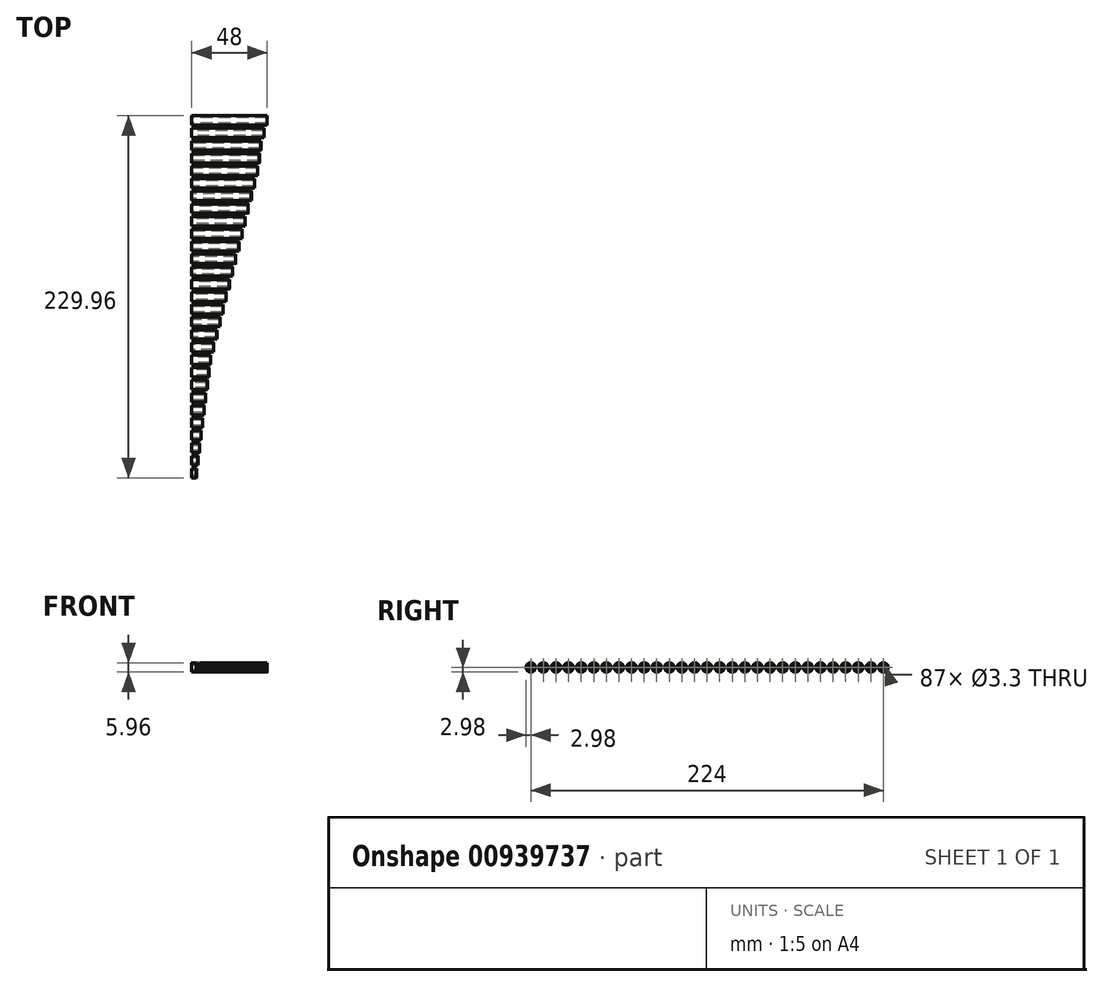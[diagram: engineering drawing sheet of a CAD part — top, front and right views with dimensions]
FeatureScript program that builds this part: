
annotation { "Feature Type Name" : "Feature", "Feature Type Description" : "" }
export const myFeature = defineFeature(function(context is Context, id is Id, definition is map)
    precondition{}
    {
        {
            var Q0;
            Q0=qCreatedBy(makeId("Right.planeOp"),FACE);
            var sketch = newSketch(context, id + "F0", { "sketchPlane" : qUnion([Q0])});
            skCircle(sketch, "E0", {"center": v(0, 0) * mm, "radius": 1.65 * mm});
            skCircle(sketch, "E1", {"center": v(0, 0) * mm, "radius": 2.98 * mm});
            skSolve(sketch);
        }
        {
            var Q0;
            Q0=qSketchRegion(id+"F0",true);
            extrude(context, id + "F1", {"entities" : qUnion([Q0]), "depth" : 3 * mm, "offsetDistance" : 25 * mm});
        }
        {
            var Q0;
            Q0=qSketchRegion(id+"F0",true);
            extrude(context, id + "F2", {"entities" : qUnion([Q0]), "depth" : 4 * mm, "offsetDistance" : 25 * mm});
        }
        {
            var Q0;
            Q0=qSketchRegion(id+"F0",true);
            extrude(context, id + "F3", {"entities" : qUnion([Q0]), "depth" : 5 * mm, "offsetDistance" : 25 * mm});
        }
        {
            var Q0;
            Q0=qSketchRegion(id+"F0",true);
            extrude(context, id + "F4", {"entities" : qUnion([Q0]), "depth" : 6 * mm, "offsetDistance" : 25 * mm});
        }
        {
            var Q0;
            Q0=qSketchRegion(id+"F0",true);
            extrude(context, id + "F5", {"entities" : qUnion([Q0]), "depth" : 7 * mm, "offsetDistance" : 25 * mm});
        }
        {
            var Q0;
            Q0=qSketchRegion(id+"F0",true);
            extrude(context, id + "F6", {"entities" : qUnion([Q0]), "depth" : 8 * mm, "offsetDistance" : 25 * mm});
        }
        {
            var Q0;
            Q0=qSketchRegion(id+"F0",true);
            extrude(context, id + "F7", {"entities" : qUnion([Q0]), "depth" : 9 * mm, "offsetDistance" : 25 * mm});
        }
        {
            var Q0;
            Q0=qSketchRegion(id+"F0",true);
            extrude(context, id + "F8", {"entities" : qUnion([Q0]), "depth" : 10 * mm, "offsetDistance" : 25 * mm});
        }
        {
            var Q0;
            Q0=qSketchRegion(id+"F0",true);
            extrude(context, id + "F9", {"entities" : qUnion([Q0]), "depth" : 11 * mm, "offsetDistance" : 25 * mm});
        }
        {
            var Q0;
            Q0=qSketchRegion(id+"F0",true);
            extrude(context, id + "F10", {"entities" : qUnion([Q0]), "depth" : 12 * mm, "offsetDistance" : 25 * mm});
        }
        {
            var Q0;
            Q0=qSketchRegion(id+"F0",true);
            extrude(context, id + "F11", {"entities" : qUnion([Q0]), "depth" : 14 * mm, "offsetDistance" : 25 * mm});
        }
        {
            var Q0;
            Q0=qSketchRegion(id+"F0",true);
            extrude(context, id + "F12", {"entities" : qUnion([Q0]), "depth" : 16 * mm, "offsetDistance" : 25 * mm});
        }
        {
            var Q0;
            Q0=qSketchRegion(id+"F0",true);
            extrude(context, id + "F13", {"entities" : qUnion([Q0]), "depth" : 18 * mm, "offsetDistance" : 25 * mm});
        }
        {
            var Q0;
            Q0=qSketchRegion(id+"F0",true);
            extrude(context, id + "F14", {"entities" : qUnion([Q0]), "depth" : 20 * mm, "offsetDistance" : 25 * mm});
        }
        {
            var Q0;
            Q0=qSketchRegion(id+"F0",true);
            extrude(context, id + "F15", {"entities" : qUnion([Q0]), "depth" : 22 * mm, "offsetDistance" : 25 * mm});
        }
        {
            var Q0;
            Q0=qSketchRegion(id+"F0",true);
            extrude(context, id + "F16", {"entities" : qUnion([Q0]), "depth" : 24 * mm, "offsetDistance" : 25 * mm});
        }
        {
            var Q0;
            Q0=qSketchRegion(id+"F0",true);
            extrude(context, id + "F17", {"entities" : qUnion([Q0]), "depth" : 26 * mm, "offsetDistance" : 25 * mm});
        }
        {
            var Q0;
            Q0=qSketchRegion(id+"F0",true);
            extrude(context, id + "F18", {"entities" : qUnion([Q0]), "depth" : 28 * mm, "offsetDistance" : 25 * mm});
        }
        {
            var Q0;
            Q0=qSketchRegion(id+"F0",true);
            extrude(context, id + "F19", {"entities" : qUnion([Q0]), "depth" : 30 * mm, "offsetDistance" : 25 * mm});
        }
        {
            var Q0;
            Q0=qSketchRegion(id+"F0",true);
            extrude(context, id + "F20", {"entities" : qUnion([Q0]), "depth" : 32 * mm, "offsetDistance" : 25 * mm});
        }
        {
            var Q0;
            Q0=qSketchRegion(id+"F0",true);
            extrude(context, id + "F21", {"entities" : qUnion([Q0]), "depth" : 34 * mm, "offsetDistance" : 25 * mm});
        }
        {
            var Q0;
            Q0=qSketchRegion(id+"F0",true);
            extrude(context, id + "F22", {"entities" : qUnion([Q0]), "depth" : 36 * mm, "offsetDistance" : 25 * mm});
        }
        {
            var Q0;
            Q0=qSketchRegion(id+"F0",true);
            extrude(context, id + "F23", {"entities" : qUnion([Q0]), "depth" : 38 * mm, "offsetDistance" : 25 * mm});
        }
        {
            var Q0;
            Q0=qSketchRegion(id+"F0",true);
            extrude(context, id + "F24", {"entities" : qUnion([Q0]), "depth" : 40 * mm, "offsetDistance" : 25 * mm});
        }
        {
            var Q0;
            Q0=qSketchRegion(id+"F0",true);
            extrude(context, id + "F25", {"entities" : qUnion([Q0]), "depth" : 42 * mm, "offsetDistance" : 25 * mm});
        }
        {
            var Q0;
            Q0=qSketchRegion(id+"F0",true);
            extrude(context, id + "F26", {"entities" : qUnion([Q0]), "depth" : 43 * mm, "offsetDistance" : 25 * mm});
        }
        {
            var Q0;
            Q0=qSketchRegion(id+"F0",true);
            extrude(context, id + "F27", {"entities" : qUnion([Q0]), "depth" : 44 * mm, "offsetDistance" : 25 * mm});
        }
        {
            var Q0;
            Q0=qSketchRegion(id+"F0",true);
            extrude(context, id + "F28", {"entities" : qUnion([Q0]), "depth" : 46 * mm, "offsetDistance" : 25 * mm});
        }
        {
            var Q0;
            Q0=qSketchRegion(id+"F0",true);
            extrude(context, id + "F29", {"entities" : qUnion([Q0]), "depth" : 48 * mm, "offsetDistance" : 25 * mm});
        }
        {
            var Q0;
            Q0=makeQuery(id+"F1.opExtrude","CAP_EDGE",EDGE,{"disambiguationData":[OSD([sQuery(id+"F0.wireOp",EDGE,"E0")])],"isStart":false});
            var Q1;
            Q1=makeQuery(id+"F2.opExtrude","SWEPT_FACE",FACE,{"disambiguationData":[OSD([sQuery(id+"F0.wireOp",EDGE,"E0")])]});
            var Q2;
            Q2=makeQuery(id+"F3.opExtrude","CAP_EDGE",EDGE,{"disambiguationData":[OSD([sQuery(id+"F0.wireOp",EDGE,"E0")])],"isStart":false});
            var Q3;
            Q3=makeQuery(id+"F1.opExtrude","CAP_EDGE",EDGE,{"disambiguationData":[OSD([sQuery(id+"F0.wireOp",EDGE,"E0")])],"isStart":true});
            var Q4;
            Q4=makeQuery(id+"F3.opExtrude","CAP_EDGE",EDGE,{"disambiguationData":[OSD([sQuery(id+"F0.wireOp",EDGE,"E0")])],"isStart":true});
            var Q5;
            Q5=makeQuery(id+"F4.opExtrude","CAP_EDGE",EDGE,{"disambiguationData":[OSD([sQuery(id+"F0.wireOp",EDGE,"E0")])],"isStart":true});
            var Q6;
            Q6=makeQuery(id+"F4.opExtrude","CAP_EDGE",EDGE,{"disambiguationData":[OSD([sQuery(id+"F0.wireOp",EDGE,"E0")])],"isStart":false});
            var Q7;
            Q7=makeQuery(id+"F5.opExtrude","CAP_EDGE",EDGE,{"disambiguationData":[OSD([sQuery(id+"F0.wireOp",EDGE,"E0")])],"isStart":false});
            var Q8;
            Q8=makeQuery(id+"F5.opExtrude","CAP_EDGE",EDGE,{"disambiguationData":[OSD([sQuery(id+"F0.wireOp",EDGE,"E0")])],"isStart":true});
            var Q9;
            Q9=makeQuery(id+"F6.opExtrude","CAP_EDGE",EDGE,{"disambiguationData":[OSD([sQuery(id+"F0.wireOp",EDGE,"E0")])],"isStart":true});
            var Q10;
            Q10=makeQuery(id+"F6.opExtrude","CAP_EDGE",EDGE,{"disambiguationData":[OSD([sQuery(id+"F0.wireOp",EDGE,"E0")])],"isStart":false});
            var Q11;
            Q11=makeQuery(id+"F7.opExtrude","CAP_EDGE",EDGE,{"disambiguationData":[OSD([sQuery(id+"F0.wireOp",EDGE,"E0")])],"isStart":false});
            var Q12;
            Q12=makeQuery(id+"F7.opExtrude","CAP_EDGE",EDGE,{"disambiguationData":[OSD([sQuery(id+"F0.wireOp",EDGE,"E0")])],"isStart":true});
            var Q13;
            Q13=makeQuery(id+"F8.opExtrude","CAP_EDGE",EDGE,{"disambiguationData":[OSD([sQuery(id+"F0.wireOp",EDGE,"E0")])],"isStart":true});
            var Q14;
            Q14=makeQuery(id+"F8.opExtrude","CAP_EDGE",EDGE,{"disambiguationData":[OSD([sQuery(id+"F0.wireOp",EDGE,"E0")])],"isStart":false});
            var Q15;
            Q15=makeQuery(id+"F9.opExtrude","CAP_EDGE",EDGE,{"disambiguationData":[OSD([sQuery(id+"F0.wireOp",EDGE,"E0")])],"isStart":false});
            var Q16;
            Q16=makeQuery(id+"F9.opExtrude","CAP_EDGE",EDGE,{"disambiguationData":[OSD([sQuery(id+"F0.wireOp",EDGE,"E0")])],"isStart":true});
            var Q17;
            Q17=makeQuery(id+"F10.opExtrude","CAP_EDGE",EDGE,{"disambiguationData":[OSD([sQuery(id+"F0.wireOp",EDGE,"E0")])],"isStart":true});
            var Q18;
            Q18=makeQuery(id+"F10.opExtrude","CAP_EDGE",EDGE,{"disambiguationData":[OSD([sQuery(id+"F0.wireOp",EDGE,"E0")])],"isStart":false});
            var Q19;
            Q19=makeQuery(id+"F11.opExtrude","CAP_EDGE",EDGE,{"disambiguationData":[OSD([sQuery(id+"F0.wireOp",EDGE,"E0")])],"isStart":false});
            var Q20;
            Q20=makeQuery(id+"F11.opExtrude","CAP_EDGE",EDGE,{"disambiguationData":[OSD([sQuery(id+"F0.wireOp",EDGE,"E0")])],"isStart":true});
            var Q21;
            Q21=makeQuery(id+"F12.opExtrude","CAP_EDGE",EDGE,{"disambiguationData":[OSD([sQuery(id+"F0.wireOp",EDGE,"E0")])],"isStart":true});
            var Q22;
            Q22=makeQuery(id+"F12.opExtrude","CAP_EDGE",EDGE,{"disambiguationData":[OSD([sQuery(id+"F0.wireOp",EDGE,"E0")])],"isStart":false});
            var Q23;
            Q23=makeQuery(id+"F13.opExtrude","CAP_EDGE",EDGE,{"disambiguationData":[OSD([sQuery(id+"F0.wireOp",EDGE,"E0")])],"isStart":false});
            var Q24;
            Q24=makeQuery(id+"F13.opExtrude","CAP_EDGE",EDGE,{"disambiguationData":[OSD([sQuery(id+"F0.wireOp",EDGE,"E0")])],"isStart":true});
            var Q25;
            Q25=makeQuery(id+"F14.opExtrude","CAP_EDGE",EDGE,{"disambiguationData":[OSD([sQuery(id+"F0.wireOp",EDGE,"E0")])],"isStart":true});
            var Q26;
            Q26=makeQuery(id+"F14.opExtrude","CAP_EDGE",EDGE,{"disambiguationData":[OSD([sQuery(id+"F0.wireOp",EDGE,"E0")])],"isStart":false});
            var Q27;
            Q27=makeQuery(id+"F15.opExtrude","CAP_EDGE",EDGE,{"disambiguationData":[OSD([sQuery(id+"F0.wireOp",EDGE,"E0")])],"isStart":false});
            var Q28;
            Q28=makeQuery(id+"F15.opExtrude","CAP_EDGE",EDGE,{"disambiguationData":[OSD([sQuery(id+"F0.wireOp",EDGE,"E0")])],"isStart":true});
            var Q29;
            Q29=makeQuery(id+"F16.opExtrude","CAP_EDGE",EDGE,{"disambiguationData":[OSD([sQuery(id+"F0.wireOp",EDGE,"E0")])],"isStart":true});
            var Q30;
            Q30=makeQuery(id+"F16.opExtrude","CAP_EDGE",EDGE,{"disambiguationData":[OSD([sQuery(id+"F0.wireOp",EDGE,"E0")])],"isStart":false});
            var Q31;
            Q31=makeQuery(id+"F17.opExtrude","CAP_EDGE",EDGE,{"disambiguationData":[OSD([sQuery(id+"F0.wireOp",EDGE,"E0")])],"isStart":false});
            var Q32;
            Q32=makeQuery(id+"F17.opExtrude","CAP_EDGE",EDGE,{"disambiguationData":[OSD([sQuery(id+"F0.wireOp",EDGE,"E0")])],"isStart":true});
            var Q33;
            Q33=makeQuery(id+"F18.opExtrude","CAP_EDGE",EDGE,{"disambiguationData":[OSD([sQuery(id+"F0.wireOp",EDGE,"E0")])],"isStart":true});
            var Q34;
            Q34=makeQuery(id+"F18.opExtrude","CAP_EDGE",EDGE,{"disambiguationData":[OSD([sQuery(id+"F0.wireOp",EDGE,"E0")])],"isStart":false});
            var Q35;
            Q35=makeQuery(id+"F19.opExtrude","CAP_EDGE",EDGE,{"disambiguationData":[OSD([sQuery(id+"F0.wireOp",EDGE,"E0")])],"isStart":false});
            var Q36;
            Q36=makeQuery(id+"F19.opExtrude","CAP_EDGE",EDGE,{"disambiguationData":[OSD([sQuery(id+"F0.wireOp",EDGE,"E0")])],"isStart":true});
            var Q37;
            Q37=makeQuery(id+"F20.opExtrude","CAP_EDGE",EDGE,{"disambiguationData":[OSD([sQuery(id+"F0.wireOp",EDGE,"E0")])],"isStart":true});
            var Q38;
            Q38=makeQuery(id+"F20.opExtrude","CAP_EDGE",EDGE,{"disambiguationData":[OSD([sQuery(id+"F0.wireOp",EDGE,"E0")])],"isStart":false});
            var Q39;
            Q39=makeQuery(id+"F21.opExtrude","CAP_EDGE",EDGE,{"disambiguationData":[OSD([sQuery(id+"F0.wireOp",EDGE,"E0")])],"isStart":false});
            var Q40;
            Q40=makeQuery(id+"F21.opExtrude","CAP_EDGE",EDGE,{"disambiguationData":[OSD([sQuery(id+"F0.wireOp",EDGE,"E0")])],"isStart":true});
            var Q41;
            Q41=makeQuery(id+"F22.opExtrude","CAP_EDGE",EDGE,{"disambiguationData":[OSD([sQuery(id+"F0.wireOp",EDGE,"E0")])],"isStart":true});
            var Q42;
            Q42=makeQuery(id+"F22.opExtrude","CAP_EDGE",EDGE,{"disambiguationData":[OSD([sQuery(id+"F0.wireOp",EDGE,"E0")])],"isStart":false});
            var Q43;
            Q43=makeQuery(id+"F23.opExtrude","CAP_EDGE",EDGE,{"disambiguationData":[OSD([sQuery(id+"F0.wireOp",EDGE,"E0")])],"isStart":false});
            var Q44;
            Q44=makeQuery(id+"F23.opExtrude","CAP_EDGE",EDGE,{"disambiguationData":[OSD([sQuery(id+"F0.wireOp",EDGE,"E0")])],"isStart":true});
            var Q45;
            Q45=makeQuery(id+"F24.opExtrude","CAP_EDGE",EDGE,{"disambiguationData":[OSD([sQuery(id+"F0.wireOp",EDGE,"E0")])],"isStart":true});
            var Q46;
            Q46=makeQuery(id+"F24.opExtrude","SWEPT_FACE",FACE,{"disambiguationData":[OSD([sQuery(id+"F0.wireOp",EDGE,"E0")])]});
            var Q47;
            Q47=makeQuery(id+"F25.opExtrude","CAP_EDGE",EDGE,{"disambiguationData":[OSD([sQuery(id+"F0.wireOp",EDGE,"E0")])],"isStart":false});
            var Q48;
            Q48=makeQuery(id+"F25.opExtrude","CAP_EDGE",EDGE,{"disambiguationData":[OSD([sQuery(id+"F0.wireOp",EDGE,"E0")])],"isStart":true});
            var Q49;
            Q49=makeQuery(id+"F26.opExtrude","CAP_EDGE",EDGE,{"disambiguationData":[OSD([sQuery(id+"F0.wireOp",EDGE,"E0")])],"isStart":true});
            var Q50;
            Q50=makeQuery(id+"F26.opExtrude","CAP_EDGE",EDGE,{"disambiguationData":[OSD([sQuery(id+"F0.wireOp",EDGE,"E0")])],"isStart":false});
            var Q51;
            Q51=makeQuery(id+"F27.opExtrude","CAP_EDGE",EDGE,{"disambiguationData":[OSD([sQuery(id+"F0.wireOp",EDGE,"E0")])],"isStart":false});
            var Q52;
            Q52=makeQuery(id+"F27.opExtrude","CAP_EDGE",EDGE,{"disambiguationData":[OSD([sQuery(id+"F0.wireOp",EDGE,"E0")])],"isStart":true});
            var Q53;
            Q53=makeQuery(id+"F28.opExtrude","CAP_EDGE",EDGE,{"disambiguationData":[OSD([sQuery(id+"F0.wireOp",EDGE,"E0")])],"isStart":true});
            var Q54;
            Q54=makeQuery(id+"F28.opExtrude","CAP_EDGE",EDGE,{"disambiguationData":[OSD([sQuery(id+"F0.wireOp",EDGE,"E0")])],"isStart":false});
            var Q55;
            Q55=makeQuery(id+"F29.opExtrude","CAP_EDGE",EDGE,{"disambiguationData":[OSD([sQuery(id+"F0.wireOp",EDGE,"E0")])],"isStart":false});
            var Q56;
            Q56=makeQuery(id+"F29.opExtrude","CAP_EDGE",EDGE,{"disambiguationData":[OSD([sQuery(id+"F0.wireOp",EDGE,"E0")])],"isStart":true});
            chamfer(context, id + "F30", {"entities" : qUnion([Q0, Q1, Q2, Q3, Q4, Q5, Q6, Q7, Q8, Q9, Q10, Q11, Q12, Q13, Q14, Q15, Q16, Q17, Q18, Q19, Q20, Q21, Q22, Q23, Q24, Q25, Q26, Q27, Q28, Q29, Q30, Q31, Q32, Q33, Q34, Q35, Q36, Q37, Q38, Q39, Q40, Q41, Q42, Q43, Q44, Q45, Q46, Q47, Q48, Q49, Q50, Q51, Q52, Q53, Q54, Q55, Q56]), "width" : 0.35 * mm, "tangentPropagation" : true});
        }
        {
            var Q0;
            Q0=makeQuery(id+"F29.opExtrude","CAP_EDGE",EDGE,{"disambiguationData":[OSD([sQuery(id+"F0.wireOp",EDGE,"E1")])],"isStart":false});
            var Q1;
            Q1=makeQuery(id+"F28.opExtrude","CAP_EDGE",EDGE,{"disambiguationData":[OSD([sQuery(id+"F0.wireOp",EDGE,"E1")])],"isStart":false});
            var Q2;
            Q2=makeQuery(id+"F27.opExtrude","CAP_EDGE",EDGE,{"disambiguationData":[OSD([sQuery(id+"F0.wireOp",EDGE,"E1")])],"isStart":false});
            var Q3;
            Q3=makeQuery(id+"F26.opExtrude","CAP_EDGE",EDGE,{"disambiguationData":[OSD([sQuery(id+"F0.wireOp",EDGE,"E1")])],"isStart":false});
            var Q4;
            Q4=makeQuery(id+"F25.opExtrude","CAP_EDGE",EDGE,{"disambiguationData":[OSD([sQuery(id+"F0.wireOp",EDGE,"E1")])],"isStart":false});
            var Q5;
            Q5=makeQuery(id+"F24.opExtrude","CAP_EDGE",EDGE,{"disambiguationData":[OSD([sQuery(id+"F0.wireOp",EDGE,"E1")])],"isStart":false});
            var Q6;
            Q6=makeQuery(id+"F23.opExtrude","CAP_EDGE",EDGE,{"disambiguationData":[OSD([sQuery(id+"F0.wireOp",EDGE,"E1")])],"isStart":false});
            var Q7;
            Q7=makeQuery(id+"F22.opExtrude","CAP_EDGE",EDGE,{"disambiguationData":[OSD([sQuery(id+"F0.wireOp",EDGE,"E1")])],"isStart":false});
            var Q8;
            Q8=makeQuery(id+"F21.opExtrude","CAP_EDGE",EDGE,{"disambiguationData":[OSD([sQuery(id+"F0.wireOp",EDGE,"E1")])],"isStart":false});
            var Q9;
            Q9=makeQuery(id+"F20.opExtrude","CAP_EDGE",EDGE,{"disambiguationData":[OSD([sQuery(id+"F0.wireOp",EDGE,"E1")])],"isStart":false});
            var Q10;
            Q10=makeQuery(id+"F19.opExtrude","CAP_EDGE",EDGE,{"disambiguationData":[OSD([sQuery(id+"F0.wireOp",EDGE,"E1")])],"isStart":false});
            var Q11;
            Q11=makeQuery(id+"F18.opExtrude","CAP_EDGE",EDGE,{"disambiguationData":[OSD([sQuery(id+"F0.wireOp",EDGE,"E1")])],"isStart":false});
            var Q12;
            Q12=makeQuery(id+"F17.opExtrude","CAP_EDGE",EDGE,{"disambiguationData":[OSD([sQuery(id+"F0.wireOp",EDGE,"E1")])],"isStart":false});
            var Q13;
            Q13=makeQuery(id+"F16.opExtrude","CAP_EDGE",EDGE,{"disambiguationData":[OSD([sQuery(id+"F0.wireOp",EDGE,"E1")])],"isStart":false});
            var Q14;
            Q14=makeQuery(id+"F15.opExtrude","CAP_EDGE",EDGE,{"disambiguationData":[OSD([sQuery(id+"F0.wireOp",EDGE,"E1")])],"isStart":false});
            var Q15;
            Q15=makeQuery(id+"F14.opExtrude","CAP_EDGE",EDGE,{"disambiguationData":[OSD([sQuery(id+"F0.wireOp",EDGE,"E1")])],"isStart":false});
            var Q16;
            Q16=makeQuery(id+"F24.opExtrude","SWEPT_FACE",FACE,{"disambiguationData":[OSD([sQuery(id+"F0.wireOp",EDGE,"E1")])]});
            var Q17;
            Q17=makeQuery(id+"F12.opExtrude","CAP_EDGE",EDGE,{"disambiguationData":[OSD([sQuery(id+"F0.wireOp",EDGE,"E1")])],"isStart":false});
            var Q18;
            Q18=makeQuery(id+"F13.opExtrude","CAP_EDGE",EDGE,{"disambiguationData":[OSD([sQuery(id+"F0.wireOp",EDGE,"E1")])],"isStart":false});
            var Q19;
            Q19=makeQuery(id+"F11.opExtrude","CAP_EDGE",EDGE,{"disambiguationData":[OSD([sQuery(id+"F0.wireOp",EDGE,"E1")])],"isStart":false});
            var Q20;
            Q20=makeQuery(id+"F10.opExtrude","CAP_EDGE",EDGE,{"disambiguationData":[OSD([sQuery(id+"F0.wireOp",EDGE,"E1")])],"isStart":false});
            var Q21;
            Q21=makeQuery(id+"F9.opExtrude","CAP_EDGE",EDGE,{"disambiguationData":[OSD([sQuery(id+"F0.wireOp",EDGE,"E1")])],"isStart":false});
            var Q22;
            Q22=makeQuery(id+"F8.opExtrude","CAP_EDGE",EDGE,{"disambiguationData":[OSD([sQuery(id+"F0.wireOp",EDGE,"E1")])],"isStart":false});
            var Q23;
            Q23=makeQuery(id+"F7.opExtrude","CAP_EDGE",EDGE,{"disambiguationData":[OSD([sQuery(id+"F0.wireOp",EDGE,"E1")])],"isStart":false});
            var Q24;
            Q24=makeQuery(id+"F6.opExtrude","CAP_EDGE",EDGE,{"disambiguationData":[OSD([sQuery(id+"F0.wireOp",EDGE,"E1")])],"isStart":false});
            var Q25;
            Q25=makeQuery(id+"F5.opExtrude","CAP_EDGE",EDGE,{"disambiguationData":[OSD([sQuery(id+"F0.wireOp",EDGE,"E1")])],"isStart":false});
            var Q26;
            Q26=makeQuery(id+"F4.opExtrude","CAP_EDGE",EDGE,{"disambiguationData":[OSD([sQuery(id+"F0.wireOp",EDGE,"E1")])],"isStart":false});
            var Q27;
            Q27=makeQuery(id+"F3.opExtrude","CAP_EDGE",EDGE,{"disambiguationData":[OSD([sQuery(id+"F0.wireOp",EDGE,"E1")])],"isStart":false});
            var Q28;
            Q28=makeQuery(id+"F2.opExtrude","CAP_EDGE",EDGE,{"disambiguationData":[OSD([sQuery(id+"F0.wireOp",EDGE,"E1")])],"isStart":false});
            var Q29;
            Q29=makeQuery(id+"F1.opExtrude","CAP_EDGE",EDGE,{"disambiguationData":[OSD([sQuery(id+"F0.wireOp",EDGE,"E1")])],"isStart":false});
            chamfer(context, id + "F31", {"entities" : qUnion([Q0, Q1, Q2, Q3, Q4, Q5, Q6, Q7, Q8, Q9, Q10, Q11, Q12, Q13, Q14, Q15, Q16, Q17, Q18, Q19, Q20, Q21, Q22, Q23, Q24, Q25, Q26, Q27, Q28, Q29]), "width" : 0.1 * mm, "tangentPropagation" : true});
        }
        {
            var Q0;
            Q0=qCreatedBy(makeId("Front.planeOp"),FACE);
            var sketch = newSketch(context, id + "F32", { "sketchPlane" : qUnion([Q0])});
            skLineSegment(sketch, "E2", {"start": v(2.9, -2.98) * mm, "end": v(0, -2.98) * mm, "construction": true});
            skLineSegment(sketch, "E3", {"start": v(0, 2.98) * mm, "end": v(2.9, 2.98) * mm, "construction": true});
            skLineSegment(sketch, "E4", {"start": v(0, 2.88) * mm, "end": v(0.1, 2.98) * mm});
            skLineSegment(sketch, "E5", {"start": v(0.1, 2.98) * mm, "end": v(0, 2.98) * mm});
            skLineSegment(sketch, "E6", {"start": v(0, 2.98) * mm, "end": v(0, 2.88) * mm});
            skLineSegment(sketch, "E7", {"start": v(0, 2.98) * mm, "end": v(0.1, 2.98) * mm});
            skLineSegment(sketch, "E8", {"start": v(0, 0) * mm, "end": v(-2.68, 0) * mm, "construction": true});
            skSolve(sketch);
        }
        {
            var Q0;
            Q0=qSketchRegion(id+"F32",true);
            var Q1;
            Q1=sQuery(id+"F32.wireOp",EDGE,"E8");
            revolve(context, id + "F33", {"operationType" : NewBodyOperationType.REMOVE, "surfaceOperationType" : NewSurfaceOperationType.NEW, "entities" : qUnion([Q0]), "axis" : qUnion([Q1]), "revolveType" : RevolveType.FULL, "oppositeDirection" : true});
        }
        {
            var Q0;
            Q0=makeQuery(id+"F2.opExtrude","SWEPT_BODY",BODY,{"disambiguationData":[OSD([sQuery(id+"F0.wireOp",EDGE,"E0"),sQuery(id+"F0.wireOp",EDGE,"E1")])]});
            transform(context, id + "F34", {"entities" : qUnion([Q0]), "transformType" : TransformType.TRANSLATION_3D, "dx" : 0 * mm, "dy" : 8 * mm, "dz" : 0 * mm, "makeCopy" : false});
        }
        {
            var Q0;
            Q0=makeQuery(id+"F3.opExtrude","SWEPT_BODY",BODY,{"disambiguationData":[OSD([sQuery(id+"F0.wireOp",EDGE,"E0"),sQuery(id+"F0.wireOp",EDGE,"E1")])]});
            transform(context, id + "F35", {"entities" : qUnion([Q0]), "transformType" : TransformType.TRANSLATION_3D, "dx" : 0 * mm, "dy" : 16 * mm, "dz" : 0 * mm, "makeCopy" : false});
        }
        {
            var Q0;
            Q0=makeQuery(id+"F4.opExtrude","SWEPT_BODY",BODY,{"disambiguationData":[OSD([sQuery(id+"F0.wireOp",EDGE,"E0"),sQuery(id+"F0.wireOp",EDGE,"E1")])]});
            transform(context, id + "F36", {"entities" : qUnion([Q0]), "transformType" : TransformType.TRANSLATION_3D, "dx" : 0 * mm, "dy" : 24 * mm, "dz" : 0 * mm, "makeCopy" : false});
        }
        {
            var Q0;
            Q0=makeQuery(id+"F5.opExtrude","SWEPT_BODY",BODY,{"disambiguationData":[OSD([sQuery(id+"F0.wireOp",EDGE,"E0"),sQuery(id+"F0.wireOp",EDGE,"E1")])]});
            transform(context, id + "F37", {"entities" : qUnion([Q0]), "transformType" : TransformType.TRANSLATION_3D, "dx" : 0 * mm, "dy" : 32 * mm, "dz" : 0 * mm, "makeCopy" : false});
        }
        {
            var Q0;
            Q0=makeQuery(id+"F6.opExtrude","SWEPT_BODY",BODY,{"disambiguationData":[OSD([sQuery(id+"F0.wireOp",EDGE,"E0"),sQuery(id+"F0.wireOp",EDGE,"E1")])]});
            transform(context, id + "F38", {"entities" : qUnion([Q0]), "transformType" : TransformType.TRANSLATION_3D, "dx" : 0 * mm, "dy" : 40 * mm, "dz" : 0 * mm, "makeCopy" : false});
        }
        {
            var Q0;
            Q0=makeQuery(id+"F7.opExtrude","SWEPT_BODY",BODY,{"disambiguationData":[OSD([sQuery(id+"F0.wireOp",EDGE,"E0"),sQuery(id+"F0.wireOp",EDGE,"E1")])]});
            transform(context, id + "F39", {"entities" : qUnion([Q0]), "transformType" : TransformType.TRANSLATION_3D, "dx" : 0 * mm, "dy" : 48 * mm, "dz" : 0 * mm, "makeCopy" : false});
        }
        {
            var Q0;
            Q0=makeQuery(id+"F8.opExtrude","SWEPT_BODY",BODY,{"disambiguationData":[OSD([sQuery(id+"F0.wireOp",EDGE,"E0"),sQuery(id+"F0.wireOp",EDGE,"E1")])]});
            transform(context, id + "F40", {"entities" : qUnion([Q0]), "transformType" : TransformType.TRANSLATION_3D, "dx" : 0 * mm, "dy" : 56 * mm, "dz" : 0 * mm, "makeCopy" : false});
        }
        {
            var Q0;
            Q0=makeQuery(id+"F9.opExtrude","SWEPT_BODY",BODY,{"disambiguationData":[OSD([sQuery(id+"F0.wireOp",EDGE,"E0"),sQuery(id+"F0.wireOp",EDGE,"E1")])]});
            transform(context, id + "F41", {"entities" : qUnion([Q0]), "transformType" : TransformType.TRANSLATION_3D, "dx" : 0 * mm, "dy" : 64 * mm, "dz" : 0 * mm, "makeCopy" : false});
        }
        {
            var Q0;
            Q0=makeQuery(id+"F10.opExtrude","SWEPT_BODY",BODY,{"disambiguationData":[OSD([sQuery(id+"F0.wireOp",EDGE,"E0"),sQuery(id+"F0.wireOp",EDGE,"E1")])]});
            transform(context, id + "F42", {"entities" : qUnion([Q0]), "transformType" : TransformType.TRANSLATION_3D, "dx" : 0 * mm, "dy" : 72 * mm, "dz" : 0 * mm, "makeCopy" : false});
        }
        {
            var Q0;
            Q0=makeQuery(id+"F11.opExtrude","SWEPT_BODY",BODY,{"disambiguationData":[OSD([sQuery(id+"F0.wireOp",EDGE,"E0"),sQuery(id+"F0.wireOp",EDGE,"E1")])]});
            transform(context, id + "F43", {"entities" : qUnion([Q0]), "transformType" : TransformType.TRANSLATION_3D, "dx" : 0 * mm, "dy" : 80 * mm, "dz" : 0 * mm, "makeCopy" : false});
        }
        {
            var Q0;
            Q0=makeQuery(id+"F12.opExtrude","SWEPT_BODY",BODY,{"disambiguationData":[OSD([sQuery(id+"F0.wireOp",EDGE,"E0"),sQuery(id+"F0.wireOp",EDGE,"E1")])]});
            transform(context, id + "F44", {"entities" : qUnion([Q0]), "transformType" : TransformType.TRANSLATION_3D, "dx" : 0 * mm, "dy" : 88 * mm, "dz" : 0 * mm, "makeCopy" : false});
        }
        {
            var Q0;
            Q0=makeQuery(id+"F13.opExtrude","SWEPT_BODY",BODY,{"disambiguationData":[OSD([sQuery(id+"F0.wireOp",EDGE,"E0"),sQuery(id+"F0.wireOp",EDGE,"E1")])]});
            transform(context, id + "F45", {"entities" : qUnion([Q0]), "transformType" : TransformType.TRANSLATION_3D, "dx" : 0 * mm, "dy" : 96 * mm, "dz" : 0 * mm, "makeCopy" : false});
        }
        {
            var Q0;
            Q0=makeQuery(id+"F14.opExtrude","SWEPT_BODY",BODY,{"disambiguationData":[OSD([sQuery(id+"F0.wireOp",EDGE,"E0"),sQuery(id+"F0.wireOp",EDGE,"E1")])]});
            transform(context, id + "F46", {"entities" : qUnion([Q0]), "transformType" : TransformType.TRANSLATION_3D, "dx" : 0 * mm, "dy" : 104 * mm, "dz" : 0 * mm, "makeCopy" : false});
        }
        {
            var Q0;
            Q0=makeQuery(id+"F15.opExtrude","SWEPT_BODY",BODY,{"disambiguationData":[OSD([sQuery(id+"F0.wireOp",EDGE,"E0"),sQuery(id+"F0.wireOp",EDGE,"E1")])]});
            transform(context, id + "F47", {"entities" : qUnion([Q0]), "transformType" : TransformType.TRANSLATION_3D, "dx" : 0 * mm, "dy" : 112 * mm, "dz" : 0 * mm, "makeCopy" : false});
        }
        {
            var Q0;
            Q0=makeQuery(id+"F16.opExtrude","SWEPT_BODY",BODY,{"disambiguationData":[OSD([sQuery(id+"F0.wireOp",EDGE,"E0"),sQuery(id+"F0.wireOp",EDGE,"E1")])]});
            transform(context, id + "F48", {"entities" : qUnion([Q0]), "transformType" : TransformType.TRANSLATION_3D, "dx" : 0 * mm, "dy" : 120 * mm, "dz" : 0 * mm, "makeCopy" : false});
        }
        {
            var Q0;
            Q0=makeQuery(id+"F17.opExtrude","SWEPT_BODY",BODY,{"disambiguationData":[OSD([sQuery(id+"F0.wireOp",EDGE,"E0"),sQuery(id+"F0.wireOp",EDGE,"E1")])]});
            transform(context, id + "F49", {"entities" : qUnion([Q0]), "transformType" : TransformType.TRANSLATION_3D, "dx" : 0 * mm, "dy" : 128 * mm, "dz" : 0 * mm, "makeCopy" : false});
        }
        {
            var Q0;
            Q0=makeQuery(id+"F18.opExtrude","SWEPT_BODY",BODY,{"disambiguationData":[OSD([sQuery(id+"F0.wireOp",EDGE,"E0"),sQuery(id+"F0.wireOp",EDGE,"E1")])]});
            transform(context, id + "F50", {"entities" : qUnion([Q0]), "transformType" : TransformType.TRANSLATION_3D, "dx" : 0 * mm, "dy" : 136 * mm, "dz" : 0 * mm, "makeCopy" : false});
        }
        {
            var Q0;
            Q0=makeQuery(id+"F19.opExtrude","SWEPT_BODY",BODY,{"disambiguationData":[OSD([sQuery(id+"F0.wireOp",EDGE,"E0"),sQuery(id+"F0.wireOp",EDGE,"E1")])]});
            transform(context, id + "F51", {"entities" : qUnion([Q0]), "transformType" : TransformType.TRANSLATION_3D, "dx" : 0 * mm, "dy" : 144 * mm, "dz" : 0 * mm, "makeCopy" : false});
        }
        {
            var Q0;
            Q0=makeQuery(id+"F20.opExtrude","SWEPT_BODY",BODY,{"disambiguationData":[OSD([sQuery(id+"F0.wireOp",EDGE,"E0"),sQuery(id+"F0.wireOp",EDGE,"E1")])]});
            transform(context, id + "F52", {"entities" : qUnion([Q0]), "transformType" : TransformType.TRANSLATION_3D, "dx" : 0 * mm, "dy" : 152 * mm, "dz" : 0 * mm, "makeCopy" : false});
        }
        {
            var Q0;
            Q0=makeQuery(id+"F21.opExtrude","SWEPT_BODY",BODY,{"disambiguationData":[OSD([sQuery(id+"F0.wireOp",EDGE,"E0"),sQuery(id+"F0.wireOp",EDGE,"E1")])]});
            transform(context, id + "F53", {"entities" : qUnion([Q0]), "transformType" : TransformType.TRANSLATION_3D, "dx" : 0 * mm, "dy" : 160 * mm, "dz" : 0 * mm, "makeCopy" : false});
        }
        {
            var Q0;
            Q0=makeQuery(id+"F22.opExtrude","SWEPT_BODY",BODY,{"disambiguationData":[OSD([sQuery(id+"F0.wireOp",EDGE,"E0"),sQuery(id+"F0.wireOp",EDGE,"E1")])]});
            transform(context, id + "F54", {"entities" : qUnion([Q0]), "transformType" : TransformType.TRANSLATION_3D, "dx" : 0 * mm, "dy" : 168 * mm, "dz" : 0 * mm, "makeCopy" : false});
        }
        {
            var Q0;
            Q0=makeQuery(id+"F23.opExtrude","SWEPT_BODY",BODY,{"disambiguationData":[OSD([sQuery(id+"F0.wireOp",EDGE,"E0"),sQuery(id+"F0.wireOp",EDGE,"E1")])]});
            transform(context, id + "F55", {"entities" : qUnion([Q0]), "transformType" : TransformType.TRANSLATION_3D, "dx" : 0 * mm, "dy" : 176 * mm, "dz" : 0 * mm, "makeCopy" : false});
        }
        {
            var Q0;
            Q0=makeQuery(id+"F24.opExtrude","SWEPT_BODY",BODY,{"disambiguationData":[OSD([sQuery(id+"F0.wireOp",EDGE,"E0"),sQuery(id+"F0.wireOp",EDGE,"E1")])]});
            transform(context, id + "F56", {"entities" : qUnion([Q0]), "transformType" : TransformType.TRANSLATION_3D, "dx" : 0 * mm, "dy" : 184 * mm, "dz" : 0 * mm, "makeCopy" : false});
        }
        {
            var Q0;
            Q0=makeQuery(id+"F25.opExtrude","SWEPT_BODY",BODY,{"disambiguationData":[OSD([sQuery(id+"F0.wireOp",EDGE,"E0"),sQuery(id+"F0.wireOp",EDGE,"E1")])]});
            transform(context, id + "F57", {"entities" : qUnion([Q0]), "transformType" : TransformType.TRANSLATION_3D, "dx" : 0 * mm, "dy" : 192 * mm, "dz" : 0 * mm, "makeCopy" : false});
        }
        {
            var Q0;
            Q0=makeQuery(id+"F26.opExtrude","SWEPT_BODY",BODY,{"disambiguationData":[OSD([sQuery(id+"F0.wireOp",EDGE,"E0"),sQuery(id+"F0.wireOp",EDGE,"E1")])]});
            transform(context, id + "F58", {"entities" : qUnion([Q0]), "transformType" : TransformType.TRANSLATION_3D, "dx" : 0 * mm, "dy" : 200 * mm, "dz" : 0 * mm, "makeCopy" : false});
        }
        {
            var Q0;
            Q0=makeQuery(id+"F27.opExtrude","SWEPT_BODY",BODY,{"disambiguationData":[OSD([sQuery(id+"F0.wireOp",EDGE,"E0"),sQuery(id+"F0.wireOp",EDGE,"E1")])]});
            transform(context, id + "F59", {"entities" : qUnion([Q0]), "transformType" : TransformType.TRANSLATION_3D, "dx" : 0 * mm, "dy" : 208 * mm, "dz" : 0 * mm, "makeCopy" : false});
        }
        {
            var Q0;
            Q0=makeQuery(id+"F28.opExtrude","SWEPT_BODY",BODY,{"disambiguationData":[OSD([sQuery(id+"F0.wireOp",EDGE,"E0"),sQuery(id+"F0.wireOp",EDGE,"E1")])]});
            transform(context, id + "F60", {"entities" : qUnion([Q0]), "transformType" : TransformType.TRANSLATION_3D, "dx" : 0 * mm, "dy" : 216 * mm, "dz" : 0 * mm, "makeCopy" : false});
        }
        {
            var Q0;
            Q0=makeQuery(id+"F29.opExtrude","SWEPT_BODY",BODY,{"disambiguationData":[OSD([sQuery(id+"F0.wireOp",EDGE,"E0"),sQuery(id+"F0.wireOp",EDGE,"E1")])]});
            transform(context, id + "F61", {"entities" : qUnion([Q0]), "transformType" : TransformType.TRANSLATION_3D, "dx" : 0 * mm, "dy" : 224 * mm, "dz" : 0 * mm, "makeCopy" : false});
        }
    });
